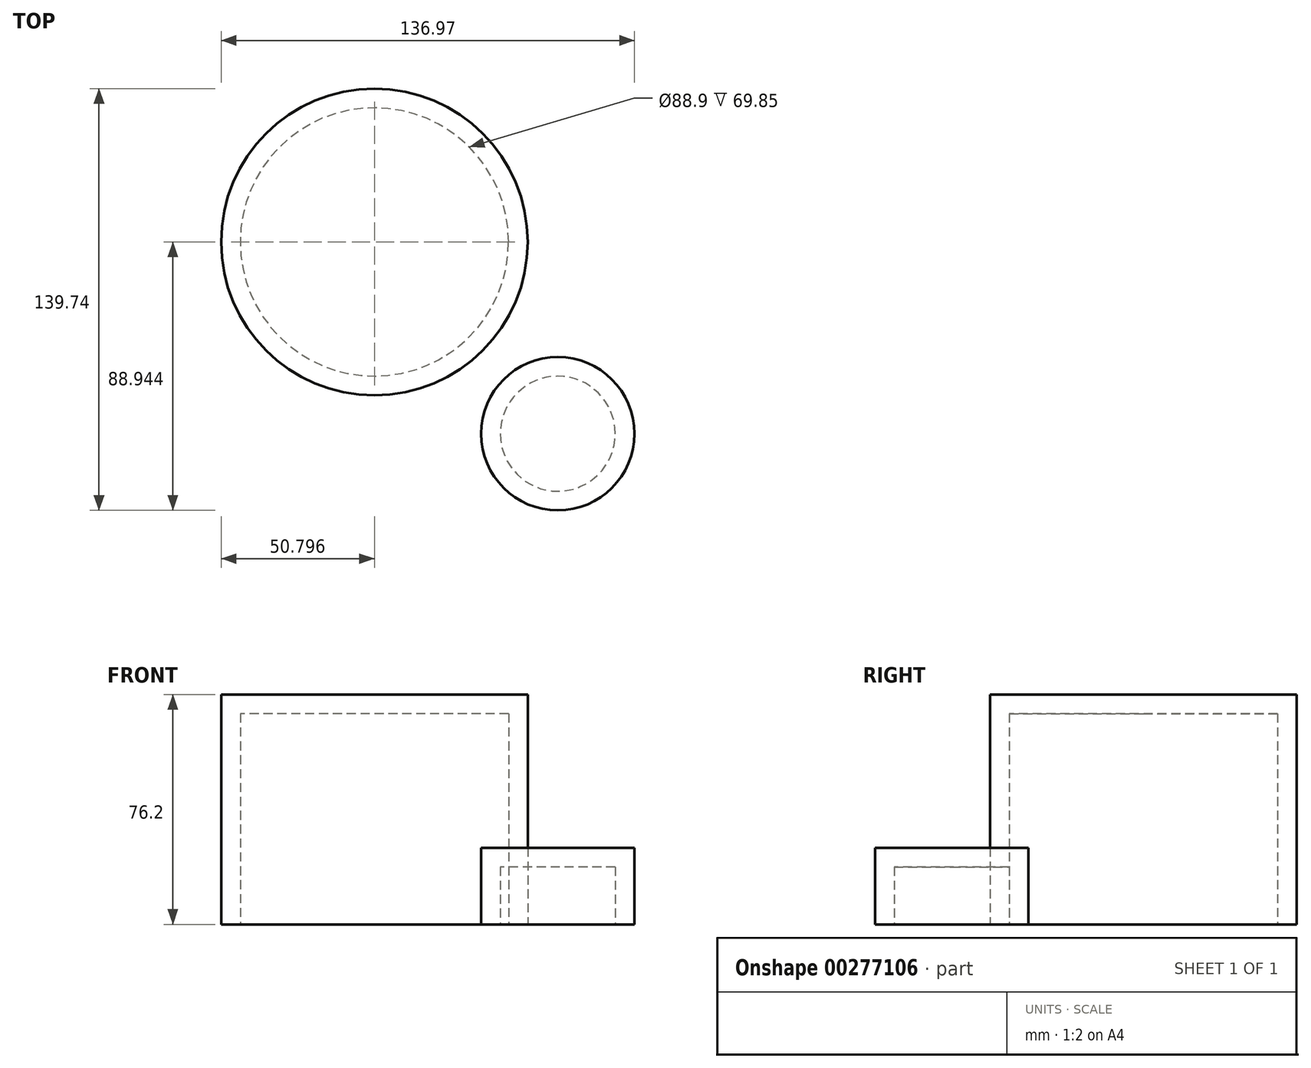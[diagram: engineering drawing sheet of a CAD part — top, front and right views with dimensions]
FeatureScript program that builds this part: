
annotation { "Feature Type Name" : "Feature", "Feature Type Description" : "" }
export const myFeature = defineFeature(function(context is Context, id is Id, definition is map)
    precondition{}
    {
        {
            var Q0;
            Q0=qCreatedBy(makeId("Top.planeOp"),FACE);
            var sketch = newSketch(context, id + "F0", { "sketchPlane" : qUnion([Q0])});
            skCircle(sketch, "E0", {"center": v(-29.33, 22.4) * mm, "radius": 50.8 * mm});
            skSolve(sketch);
        }
        {
            var Q0;
            Q0=qCreatedBy(makeId("Top.planeOp"),FACE);
            var sketch = newSketch(context, id + "F1", { "sketchPlane" : qUnion([Q0])});
            skCircle(sketch, "E1", {"center": v(31.44, -41.15) * mm, "radius": 25.4 * mm});
            skSolve(sketch);
        }
        {
            var Q0;
            Q0 = qSketchRegion(id + "F0", true);
            extrude(context, id + "F2", {"entities" : qUnion([Q0]), "depth" : 76.2 * mm});
        }
        {
            var Q0;
            Q0 = qSketchRegion(id + "F1", true);
            extrude(context, id + "F3", {"entities" : qUnion([Q0]), "depth" : 25.4 * mm});
        }
        {
            var Q0;
            Q0=makeQuery(id+"F2.opExtrude","CAP_FACE",FACE,{"disambiguationData":[OSD([sQuery(id+"F0.wireOp",EDGE,"E0")])],"isStart":true});
            shell(context, id + "F4", {"entities" : qUnion([Q0]), "thickness" : 6.35 * mm});
        }
        {
            var Q0;
            Q0=makeQuery(id+"F3.opExtrude","CAP_FACE",FACE,{"disambiguationData":[OSD([sQuery(id+"F1.wireOp",EDGE,"E1")])],"isStart":true});
            shell(context, id + "F5", {"entities" : qUnion([Q0]), "thickness" : 6.35 * mm});
        }
    });
